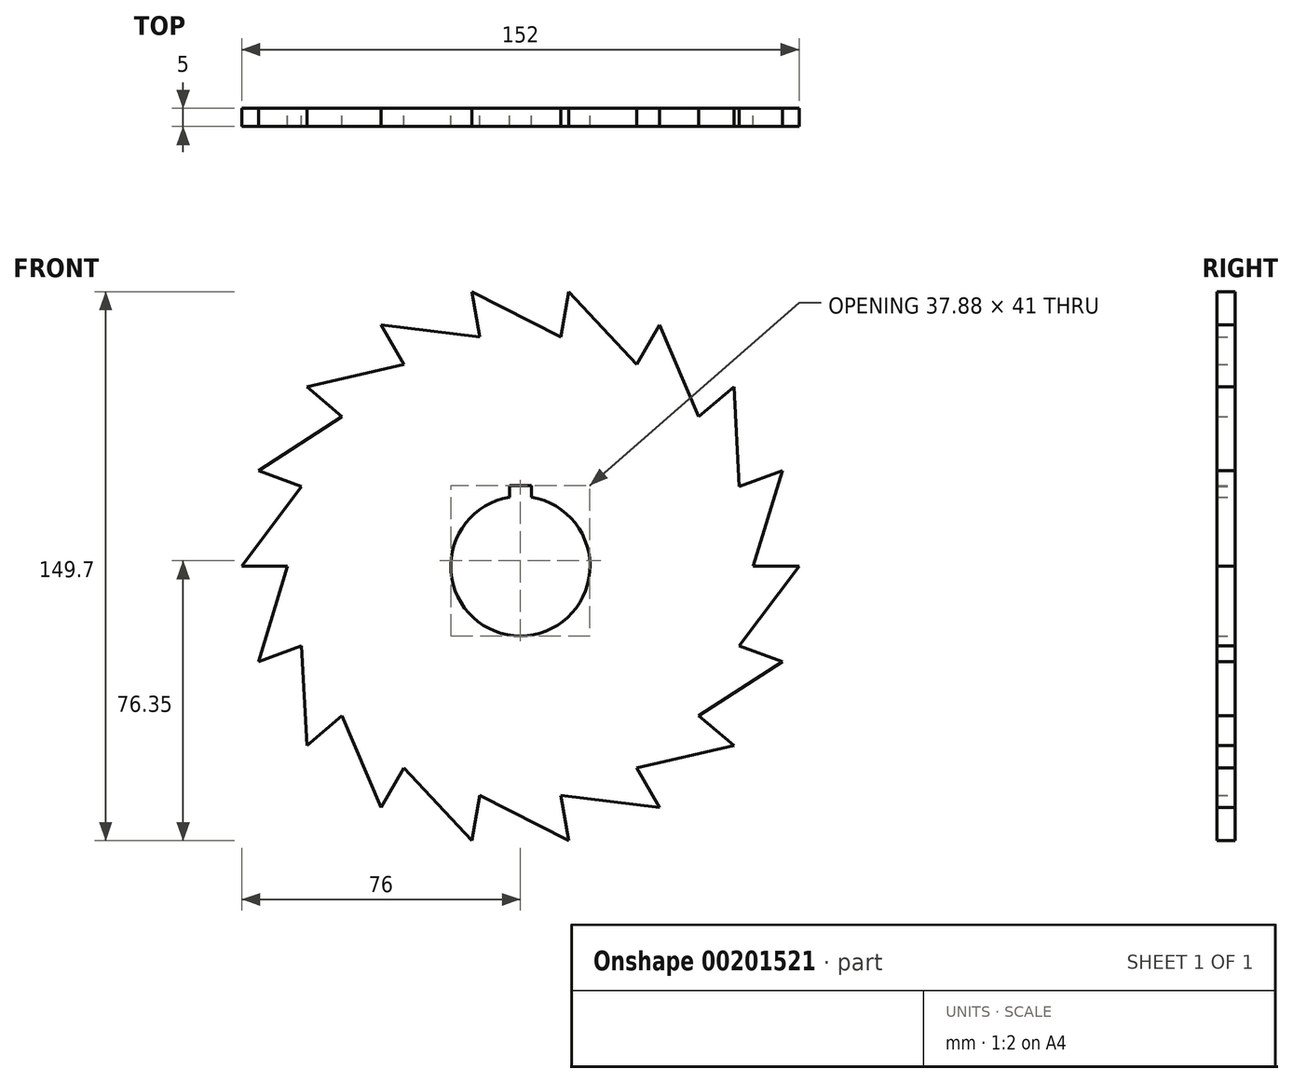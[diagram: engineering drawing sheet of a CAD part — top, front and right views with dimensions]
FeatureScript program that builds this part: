
annotation { "Feature Type Name" : "Feature", "Feature Type Description" : "" }
export const myFeature = defineFeature(function(context is Context, id is Id, definition is map)
    precondition{}
    {
        {
            var Q0;
            Q0=qCreatedBy(makeId("Front.planeOp"),FACE);
            var sketch = newSketch(context, id + "F0", { "sketchPlane" : qUnion([Q0])});
            skCircle(sketch, "E0", {"center": v(0, 0) * mm, "radius": 19 * mm});
            skCircle(sketch, "E1", {"center": v(0, 0) * mm, "radius": 63.5 * mm, "construction": true});
            skLineSegment(sketch, "E2.bottom", {"start": v(-3, 22) * mm, "end": v(3, 22) * mm});
            skLineSegment(sketch, "E2.top", {"start": v(-3, 15) * mm, "end": v(3, 15) * mm});
            skLineSegment(sketch, "E2.left", {"start": v(-3, 22) * mm, "end": v(-3, 15) * mm});
            skLineSegment(sketch, "E2.right", {"start": v(3, 22) * mm, "end": v(3, 15) * mm});
            skLineSegment(sketch, "E3", {"start": v(0, 0) * mm, "end": v(79.72, 29.02) * mm, "construction": true});
            skLineSegment(sketch, "E4", {"start": v(59.67, 21.72) * mm, "end": v(71.42, 26) * mm});
            skLineSegment(sketch, "E5", {"start": v(71.42, 26) * mm, "end": v(63.5, 0) * mm});
            skCircle(sketch, "E6", {"center": v(0, 0) * mm, "radius": 76 * mm, "construction": true});
            skLineSegment(sketch, "E7.1.0", {"start": v(48.64, 40.82) * mm, "end": v(58.22, 48.85) * mm});
            skLineSegment(sketch, "E7.1.1", {"start": v(58.22, 48.85) * mm, "end": v(59.67, 21.72) * mm});
            skLineSegment(sketch, "E7.2.0", {"start": v(31.75, 55) * mm, "end": v(38, 65.82) * mm});
            skLineSegment(sketch, "E7.2.1", {"start": v(38, 65.82) * mm, "end": v(48.64, 40.82) * mm});
            skLineSegment(sketch, "E8.1.3.0", {"start": v(11.03, 62.54) * mm, "end": v(13.2, 74.85) * mm});
            skLineSegment(sketch, "E8.3.3.0", {"start": v(13.2, 74.85) * mm, "end": v(31.75, 55) * mm});
            skLineSegment(sketch, "E8.1.4.0", {"start": v(-11.03, 62.54) * mm, "end": v(-13.2, 74.85) * mm});
            skLineSegment(sketch, "E8.3.4.0", {"start": v(-13.2, 74.85) * mm, "end": v(11.03, 62.54) * mm});
            skLineSegment(sketch, "E8.1.5.0", {"start": v(-31.75, 55) * mm, "end": v(-38, 65.82) * mm});
            skLineSegment(sketch, "E8.3.5.0", {"start": v(-38, 65.82) * mm, "end": v(-11.03, 62.54) * mm});
            skLineSegment(sketch, "E8.1.6.0", {"start": v(-48.64, 40.82) * mm, "end": v(-58.22, 48.85) * mm});
            skLineSegment(sketch, "E8.3.6.0", {"start": v(-58.22, 48.85) * mm, "end": v(-31.75, 55) * mm});
            skLineSegment(sketch, "E8.1.7.0", {"start": v(-59.67, 21.72) * mm, "end": v(-71.42, 26) * mm});
            skLineSegment(sketch, "E8.3.7.0", {"start": v(-71.42, 26) * mm, "end": v(-48.64, 40.82) * mm});
            skLineSegment(sketch, "E8.1.8.0", {"start": v(-63.5, 0) * mm, "end": v(-76, 0) * mm});
            skLineSegment(sketch, "E8.3.8.0", {"start": v(-76, 0) * mm, "end": v(-59.67, 21.72) * mm});
            skLineSegment(sketch, "E8.1.9.0", {"start": v(-59.67, -21.72) * mm, "end": v(-71.42, -26) * mm});
            skLineSegment(sketch, "E8.3.9.0", {"start": v(-71.42, -26) * mm, "end": v(-63.5, 0) * mm});
            skLineSegment(sketch, "E8.1.10.0", {"start": v(-48.64, -40.82) * mm, "end": v(-58.22, -48.85) * mm});
            skLineSegment(sketch, "E8.3.10.0", {"start": v(-58.22, -48.85) * mm, "end": v(-59.67, -21.72) * mm});
            skLineSegment(sketch, "E8.1.11.0", {"start": v(-31.75, -55) * mm, "end": v(-38, -65.82) * mm});
            skLineSegment(sketch, "E8.3.11.0", {"start": v(-38, -65.82) * mm, "end": v(-48.64, -40.82) * mm});
            skLineSegment(sketch, "E8.1.12.0", {"start": v(-11.03, -62.54) * mm, "end": v(-13.2, -74.85) * mm});
            skLineSegment(sketch, "E8.3.12.0", {"start": v(-13.2, -74.85) * mm, "end": v(-31.75, -55) * mm});
            skLineSegment(sketch, "E8.1.13.0", {"start": v(11.03, -62.54) * mm, "end": v(13.2, -74.85) * mm});
            skLineSegment(sketch, "E8.3.13.0", {"start": v(13.2, -74.85) * mm, "end": v(-11.03, -62.54) * mm});
            skLineSegment(sketch, "E8.1.14.0", {"start": v(31.75, -55) * mm, "end": v(38, -65.82) * mm});
            skLineSegment(sketch, "E8.3.14.0", {"start": v(38, -65.82) * mm, "end": v(11.03, -62.54) * mm});
            skLineSegment(sketch, "E8.1.15.0", {"start": v(48.64, -40.82) * mm, "end": v(58.22, -48.85) * mm});
            skLineSegment(sketch, "E8.3.15.0", {"start": v(58.22, -48.85) * mm, "end": v(31.75, -55) * mm});
            skLineSegment(sketch, "E8.1.16.0", {"start": v(59.67, -21.72) * mm, "end": v(71.42, -26) * mm});
            skLineSegment(sketch, "E8.3.16.0", {"start": v(71.42, -26) * mm, "end": v(48.64, -40.82) * mm});
            skLineSegment(sketch, "E8.1.17.0", {"start": v(63.5, 0) * mm, "end": v(76, 0) * mm});
            skLineSegment(sketch, "E8.3.17.0", {"start": v(76, 0) * mm, "end": v(59.67, -21.72) * mm});
            skSolve(sketch);
        }
        {
            var Q0;
            {var subQ1=sQuery(id+"F0.wireOp",EDGE,"E2.bottom");Q0=makeQuery(id+"F0.imprint","IMPRINT",FACE,{"disambiguationData":[TD([[makeQuery(id+"F0.imprint","IMPRINT",EDGE,{"derivedFrom":subQ1}),1.0]])]});}
            extrude(context, id + "F1", {"entities" : qUnion([Q0]), "depth" : 5 * mm});
        }
    });
